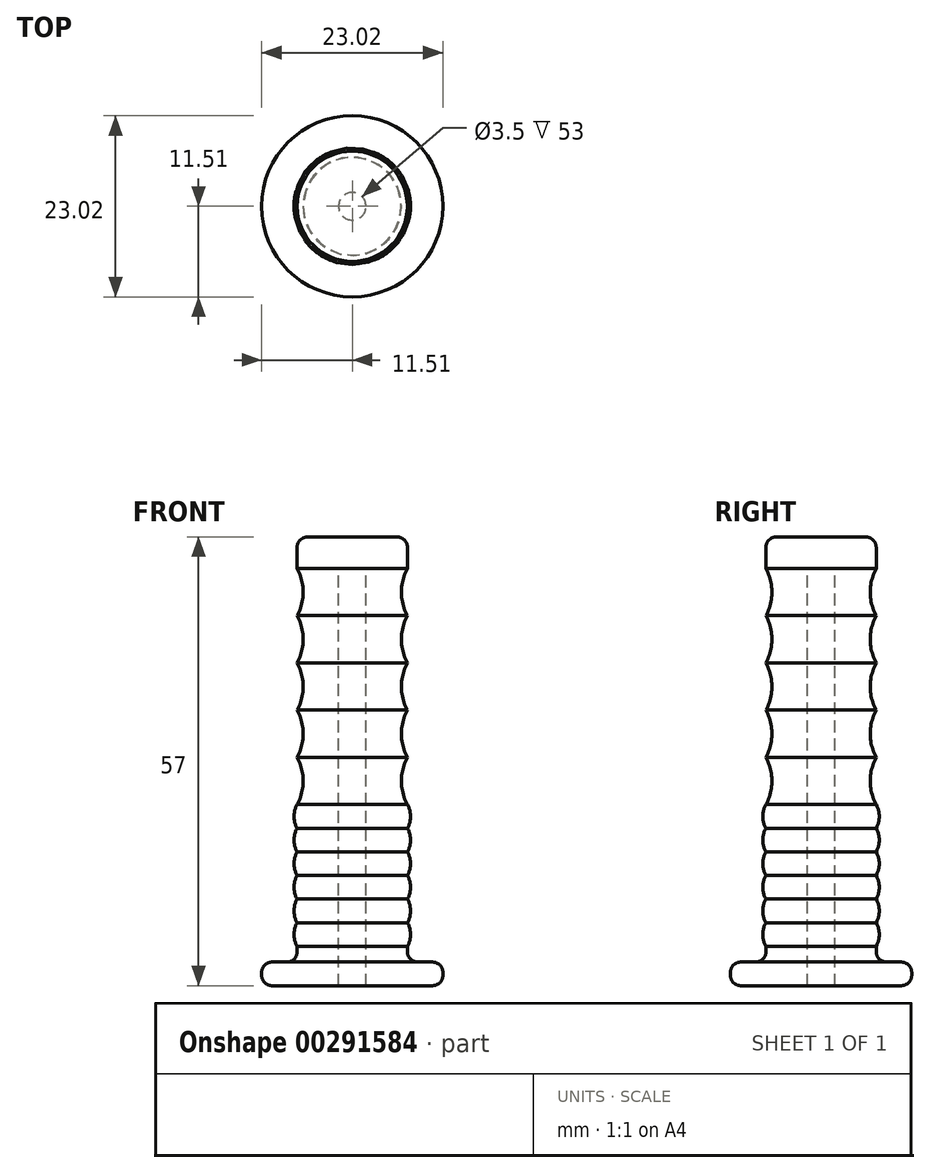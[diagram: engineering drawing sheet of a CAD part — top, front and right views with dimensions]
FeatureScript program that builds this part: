
annotation { "Feature Type Name" : "Feature", "Feature Type Description" : "" }
export const myFeature = defineFeature(function(context is Context, id is Id, definition is map)
    precondition{}
    {
        {
            assignVariable(context, id + "F0", {"name" : "dicke", "anyValue" : 50});
        }
        {
            var Q0;
            Q0=qCreatedBy(makeId("Top.planeOp"),FACE);
            var sketch = newSketch(context, id + "F1", { "sketchPlane" : qUnion([Q0])});
            skCircle(sketch, "E0", {"center": v(0, 0) * mm, "radius": 7 * mm});
            skSolve(sketch);
        }
        {
            var Q0;
            Q0=makeQuery(id+"F1.imprint","IMPRINT",FACE,{"disambiguationData":[TD([[makeQuery(id+"F1.imprint","IMPRINT",EDGE,{"derivedFrom":sQuery(id+"F1.wireOp",EDGE,"E0")}),1.0]])]});
            extrude(context, id + "F2", {"entities" : qUnion([Q0]), "endBound" : BoundingType.SYMMETRIC, "depth" : (getVariable(context, 'dicke')) * mm});
        }
        {
            var Q0;
            Q0=qCreatedBy(makeId("Top.planeOp"),FACE);
            var sketch = newSketch(context, id + "F3", { "sketchPlane" : qUnion([Q0])});
            skCircle(sketch, "E1", {"center": v(0, 0) * mm, "radius": 1.75 * mm});
            skSolve(sketch);
        }
        {
            var Q0;
            Q0 = qSketchRegion(id + "F3", true);
            extrude(context, id + "F4", {"entities" : qUnion([Q0]), "operationType" : NewBodyOperationType.REMOVE, "endBound" : BoundingType.SYMMETRIC, "oppositeDirection" : true, "depth" : (getVariable(context, 'dicke')) * mm});
        }
        {
            var Q0;
            Q0=qCreatedBy(makeId("Right.planeOp"),FACE);
            var sketch = newSketch(context, id + "F5", { "sketchPlane" : qUnion([Q0])});
            skLineSegment(sketch, "E2.0", {"start": v(-1.75, 0) * mm, "end": v(1.75, 0) * mm});
            skLineSegment(sketch, "E2.1", {"start": v(-7, 0) * mm, "end": v(7, 0) * mm});
            skLineSegment(sketch, "E3.0", {"start": v(-7, 25) * mm, "end": v(7, 25) * mm});
            skArc(sketch, "E4", {"start": v(7, 25) * mm, "mid": v(6.25, 22) * mm, "end": v(7, 19) * mm});
            skArc(sketch, "E5.0.1.0", {"start": v(7, 19) * mm, "mid": v(6.25, 16) * mm, "end": v(7, 13) * mm});
            skArc(sketch, "E5.0.2.0", {"start": v(7, 13) * mm, "mid": v(6.25, 10) * mm, "end": v(7, 7) * mm});
            skArc(sketch, "E5.0.3.0", {"start": v(7, 7) * mm, "mid": v(6.25, 4) * mm, "end": v(7, 1) * mm});
            skArc(sketch, "E5.0.4.0", {"start": v(7, 1) * mm, "mid": v(6.25, -2) * mm, "end": v(7, -5) * mm});
            skLineSegment(sketch, "E5.direction1", {"start": v(7, 19) * mm, "end": v(32, 19) * mm, "construction": true});
            skLineSegment(sketch, "E5.direction2", {"start": v(7, 19) * mm, "end": v(7, 13) * mm, "construction": true});
            skLineSegment(sketch, "E6", {"start": v(7, 25) * mm, "end": v(7, 19) * mm});
            skLineSegment(sketch, "E7", {"start": v(7, 19) * mm, "end": v(7, 13) * mm});
            skLineSegment(sketch, "E8", {"start": v(7, 13) * mm, "end": v(7, 7) * mm});
            skLineSegment(sketch, "E9", {"start": v(7, 7) * mm, "end": v(7, 1) * mm});
            skLineSegment(sketch, "E10", {"start": v(7, 1) * mm, "end": v(7, -5) * mm});
            skLineSegment(sketch, "E11", {"start": v(0, 30.34) * mm, "end": v(0, -4.22) * mm, "construction": true});
            skSolve(sketch);
        }
        {
            var Q0;
            Q0 = qSketchRegion(id + "F5", true);
            var Q1;
            Q1=sQuery(id+"F5.wireOp",EDGE,"E11");
            revolve(context, id + "F6", {"operationType" : NewBodyOperationType.REMOVE, "entities" : qUnion([Q0]), "axis" : qUnion([Q1]), "revolveType" : RevolveType.FULL, "oppositeDirection" : true});
        }
        {
            var Q0;
            Q0=qCreatedBy(makeId("Right.planeOp"),FACE);
            var sketch = newSketch(context, id + "F7", { "sketchPlane" : qUnion([Q0])});
            skLineSegment(sketch, "E12.0", {"start": v(-7, -25) * mm, "end": v(7, -25) * mm});
            skLineSegment(sketch, "E13.0", {"start": v(7, -5) * mm, "end": v(-7, -5) * mm});
            skLineSegment(sketch, "E14.0", {"start": v(7, 1) * mm, "end": v(-7, 1) * mm});
            skArc(sketch, "E15", {"start": v(7, -8) * mm, "mid": v(7.4, -6.5) * mm, "end": v(7, -5) * mm});
            skArc(sketch, "E16.0.1.0", {"start": v(7, -11) * mm, "mid": v(7.4, -9.5) * mm, "end": v(7, -8) * mm});
            skArc(sketch, "E16.0.2.0", {"start": v(7, -14) * mm, "mid": v(7.4, -12.5) * mm, "end": v(7, -11) * mm});
            skArc(sketch, "E16.0.3.0", {"start": v(7, -17) * mm, "mid": v(7.4, -15.5) * mm, "end": v(7, -14) * mm});
            skArc(sketch, "E16.0.4.0", {"start": v(7, -20) * mm, "mid": v(7.4, -18.5) * mm, "end": v(7, -17) * mm});
            skArc(sketch, "E16.0.5.0", {"start": v(7, -23) * mm, "mid": v(7.4, -21.5) * mm, "end": v(7, -20) * mm});
            skLineSegment(sketch, "E16.direction1", {"start": v(4.38, -6.5) * mm, "end": v(29.38, -6.5) * mm, "construction": true});
            skLineSegment(sketch, "E16.direction2", {"start": v(4.38, -6.5) * mm, "end": v(4.38, -9.5) * mm, "construction": true});
            skLineSegment(sketch, "E17", {"start": v(7, -5) * mm, "end": v(7, -8) * mm});
            skLineSegment(sketch, "E18", {"start": v(7, -8) * mm, "end": v(7, -11) * mm});
            skLineSegment(sketch, "E19", {"start": v(7, -11) * mm, "end": v(7, -14) * mm});
            skLineSegment(sketch, "E20", {"start": v(7, -14) * mm, "end": v(7, -17) * mm});
            skLineSegment(sketch, "E21", {"start": v(7, -17) * mm, "end": v(7, -20) * mm});
            skLineSegment(sketch, "E22", {"start": v(7, -20) * mm, "end": v(7, -23) * mm});
            skLineSegment(sketch, "E23", {"start": v(0, 0) * mm, "end": v(0, -18.46) * mm, "construction": true});
            skSolve(sketch);
        }
        {
            var Q0;
            Q0 = qSketchRegion(id + "F7", true);
            var Q1;
            Q1=sQuery(id+"F7.wireOp",EDGE,"E23");
            revolve(context, id + "F8", {"operationType" : NewBodyOperationType.ADD, "entities" : qUnion([Q0]), "axis" : qUnion([Q1]), "revolveType" : RevolveType.FULL});
        }
        {
            var Q0;
            Q0=makeQuery(id+"F2.opExtrude","CAP_FACE",FACE,{"disambiguationData":[OSD([sQuery(id+"F1.wireOp",EDGE,"E0")])],"isStart":false});
            var sketch = newSketch(context, id + "F9", { "sketchPlane" : qUnion([Q0])});
            skCircle(sketch, "E24.0", {"center": v(0, 0) * mm, "radius": 7 * mm});
            skSolve(sketch);
        }
        {
            var Q0;
            Q0 = qSketchRegion(id + "F9", true);
            var Q1;
            Q1=makeQuery(id+"F9.imprint","IMPRINT",FACE,{"disambiguationData":[TD([[makeQuery(id+"F9.imprint","IMPRINT",EDGE,{"derivedFrom":makeQuery(id+"F4.boolean.opBoolean","COPY",EDGE,{"derivedFrom":makeQuery(id+"F4.opExtrude","CAP_EDGE",EDGE,{"disambiguationData":[OSD([sQuery(id+"F3.wireOp",EDGE,"E1")])],"isStart":true})})}),1.0]])]});
            var Q2;
            Q2=makeQuery(id+"F9.imprint","IMPRINT",FACE,{"disambiguationData":[TD([[makeQuery(id+"F9.imprint","IMPRINT",EDGE,{"derivedFrom":sQuery(id+"F9.wireOp",EDGE,"E24.0")}),-1.0]])]});
            extrude(context, id + "F10", {"entities" : qUnion([Q0, Q1, Q2]), "operationType" : NewBodyOperationType.ADD, "depth" : 4 * mm});
        }
        {
            var Q0;
            Q0=makeQuery(id+"F2.opExtrude","CAP_FACE",FACE,{"disambiguationData":[OSD([sQuery(id+"F1.wireOp",EDGE,"E0")])],"isStart":true});
            var sketch = newSketch(context, id + "F11", { "sketchPlane" : qUnion([Q0])});
            skCircle(sketch, "E25.0", {"center": v(0, 0) * mm, "radius": 1.75 * mm});
            skCircle(sketch, "E26", {"center": v(0, 0) * mm, "radius": 11.5 * mm});
            skSolve(sketch);
        }
        {
            var Q0;
            Q0 = qSketchRegion(id + "F11", true);
            extrude(context, id + "F12", {"entities" : qUnion([Q0]), "operationType" : NewBodyOperationType.ADD, "depth" : 3 * mm});
        }
        {
            var Q0;
            Q0=makeQuery(id+"F12.opExtrude","CAP_FACE",FACE,{"disambiguationData":[OSD([sQuery(id+"F11.wireOp",EDGE,"E25.0"),sQuery(id+"F11.wireOp",EDGE,"E26")])],"isStart":true});
            var Q1;
            Q1=makeQuery(id+"F12.opExtrude","CAP_EDGE",EDGE,{"disambiguationData":[OSD([sQuery(id+"F11.wireOp",EDGE,"E26")])],"isStart":false});
            var Q2;
            Q2=makeQuery(id+"F10.opExtrude","CAP_EDGE",EDGE,{"disambiguationData":[OSD([sQuery(id+"F9.wireOp",EDGE,"E24.0")])],"isStart":false});
            fillet(context, id + "F13", {"entities" : qUnion([Q0, Q1, Q2]), "radius" : 1.3 * mm, "tangentPropagation" : true, "allowEdgeOverflow" : false});
        }
    });
